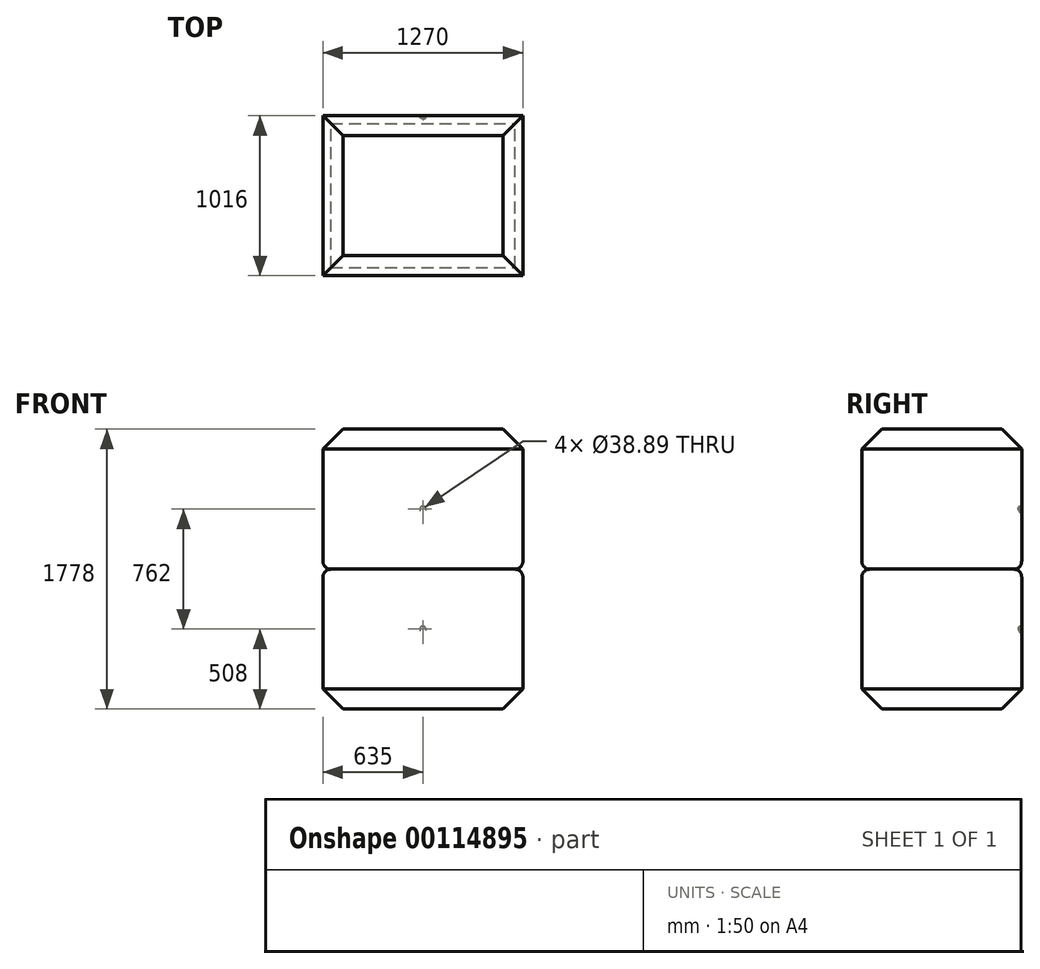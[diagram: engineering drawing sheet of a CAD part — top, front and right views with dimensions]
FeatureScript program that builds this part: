
annotation { "Feature Type Name" : "Feature", "Feature Type Description" : "" }
export const myFeature = defineFeature(function(context is Context, id is Id, definition is map)
    precondition{}
    {
        {
            var Q0;
            Q0=qCreatedBy(makeId("Top.planeOp"),FACE);
            var sketch = newSketch(context, id + "F0", { "sketchPlane" : qUnion([Q0])});
            skLineSegment(sketch, "E0.bottom", {"start": v(0, 0) * mm, "end": v(1270, 0) * mm});
            skLineSegment(sketch, "E0.top", {"start": v(0, 1016) * mm, "end": v(1270, 1016) * mm});
            skLineSegment(sketch, "E0.left", {"start": v(0, 0) * mm, "end": v(0, 1016) * mm});
            skLineSegment(sketch, "E0.right", {"start": v(1270, 0) * mm, "end": v(1270, 1016) * mm});
            skSolve(sketch);
        }
        {
            var Q0;
            Q0=makeQuery(id+"F0.imprint","IMPRINT",FACE,{"disambiguationData":[TD([[makeQuery(id+"F0.imprint","IMPRINT",EDGE,{"derivedFrom":sQuery(id+"F0.wireOp",EDGE,"E0.bottom")}),1.0]])]});
            extrude(context, id + "F1", {"entities" : qUnion([Q0]), "depth" : 889 * mm});
        }
        {
            var Q0;
            Q0=makeQuery(id+"F1.opExtrude","CAP_EDGE",EDGE,{"disambiguationData":[OSD([sQuery(id+"F0.wireOp",EDGE,"E0.right")])],"isStart":false});
            var Q1;
            Q1=makeQuery(id+"F1.opExtrude","CAP_EDGE",EDGE,{"disambiguationData":[OSD([sQuery(id+"F0.wireOp",EDGE,"E0.top")])],"isStart":false});
            var Q2;
            Q2=makeQuery(id+"F1.opExtrude","CAP_EDGE",EDGE,{"disambiguationData":[OSD([sQuery(id+"F0.wireOp",EDGE,"E0.left")])],"isStart":false});
            var Q3;
            Q3=makeQuery(id+"F1.opExtrude","CAP_EDGE",EDGE,{"disambiguationData":[OSD([sQuery(id+"F0.wireOp",EDGE,"E0.bottom")])],"isStart":false});
            fillet(context, id + "F2", {"entities" : qUnion([Q0, Q1, Q2, Q3]), "radius" : 50.8 * mm, "tangentPropagation" : true, "allowEdgeOverflow" : false});
        }
        {
            var Q0;
            Q0=makeQuery(id+"F1.opExtrude","CAP_FACE",FACE,{"disambiguationData":[OSD([sQuery(id+"F0.wireOp",EDGE,"E0.bottom"),sQuery(id+"F0.wireOp",EDGE,"E0.top"),sQuery(id+"F0.wireOp",EDGE,"E0.left"),sQuery(id+"F0.wireOp",EDGE,"E0.right")])],"isStart":true});
            chamfer(context, id + "F3", {"entities" : qUnion([Q0]), "width" : 127 * mm, "tangentPropagation" : true});
        }
        {
            var Q0;
            Q0=makeQuery(id+"F1.opExtrude","SWEPT_FACE",FACE,{"disambiguationData":[OSD([sQuery(id+"F0.wireOp",EDGE,"E0.top")])]});
            var sketch = newSketch(context, id + "F4", { "sketchPlane" : qUnion([Q0])});
            skPoint(sketch, "E1", {"position": v(-635, 508) * mm});
            skSolve(sketch);
        }
        {
            var Q0;
            Q0=sQuery(id+"F4.wireOp",VERTEX,"E1");
            var Q1;
            Q1=makeQuery(id+"F1.opExtrude","SWEPT_BODY",BODY,{"disambiguationData":[OSD([sQuery(id+"F0.wireOp",EDGE,"E0.bottom"),sQuery(id+"F0.wireOp",EDGE,"E0.top"),sQuery(id+"F0.wireOp",EDGE,"E0.left"),sQuery(id+"F0.wireOp",EDGE,"E0.right")])]});
            hole(context, id + "F5", {"style" : HoleStyle.SIMPLE, "endStyle" : HoleEndStyle.BLIND, "standardTappedOrClearance" : lookupTablePath({ "standard" : "ANSI", "fit" : "Normal (ASME)", "size" : "1 1/2", "type" : "Clearance" }), "standardBlindInLast" : lookupTablePath({ "fit" : "Free", "standard" : "ANSI", "size" : "1 1/2", "type" : "Clearance" }), "holeDiameter" : 38.9 * mm, "holeDepth" : 12.7 * mm, "startFromSketch" : true, "locations" : qUnion([Q0]), "scope" : qUnion([Q1])});
        }
        {
            var Q0;
            Q0=makeQuery(id+"F1.opExtrude","SWEPT_BODY",BODY,{"disambiguationData":[OSD([sQuery(id+"F0.wireOp",EDGE,"E0.bottom"),sQuery(id+"F0.wireOp",EDGE,"E0.top"),sQuery(id+"F0.wireOp",EDGE,"E0.left"),sQuery(id+"F0.wireOp",EDGE,"E0.right")])]});
            var Q1;
            Q1=makeQuery(id+"F1.opExtrude","CAP_FACE",FACE,{"disambiguationData":[OSD([sQuery(id+"F0.wireOp",EDGE,"E0.bottom"),sQuery(id+"F0.wireOp",EDGE,"E0.top"),sQuery(id+"F0.wireOp",EDGE,"E0.left"),sQuery(id+"F0.wireOp",EDGE,"E0.right")])],"isStart":false});
            mirror(context, id + "F6", {"operationType" : NewBodyOperationType.ADD, "entities" : qUnion([Q0]), "mirrorPlane" : qUnion([Q1])});
        }
        {
            var Q0;
            Q0=makeQuery(id+"F1.opExtrude","SWEPT_BODY",BODY,{"disambiguationData":[OSD([sQuery(id+"F0.wireOp",EDGE,"E0.bottom"),sQuery(id+"F0.wireOp",EDGE,"E0.top"),sQuery(id+"F0.wireOp",EDGE,"E0.left"),sQuery(id+"F0.wireOp",EDGE,"E0.right")])]});
            transform(context, id + "F7", {"entities" : qUnion([Q0]), "transformType" : TransformType.TRANSLATION_3D, "dx" : 0 * mm, "dy" : 0 * mm, "dz" : 0 * mm, "makeCopy" : true});
        }
    });
